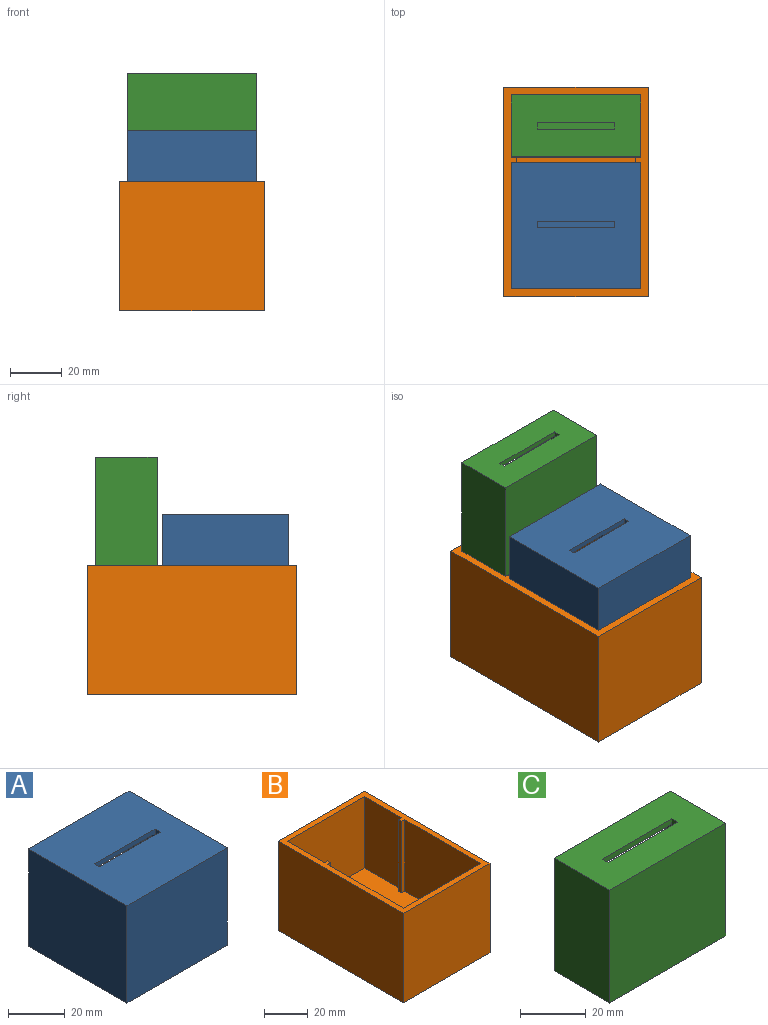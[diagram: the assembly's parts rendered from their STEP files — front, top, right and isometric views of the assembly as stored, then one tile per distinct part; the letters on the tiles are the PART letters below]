
ASSEMBLY  parts=3 mates=2
PART A: 15 faces, bbox 50x49x42 mm
  f0: plane 50x49mm, normal (0,0,1), area 2375mm2, adj f2,f3,f4,f5,f11,f12,f13,f14
  f1: plane 47x46mm, normal (0,0,-1), area 2087mm2, adj f2,f7,f8,f9,f11,f12,f13,f14
  f2: plane 50x42mm, normal (0,1,0), area 352mm2, adj f0,f1,f3,f5,f6,f7,f9,f10
  f3: plane 49x42mm, normal (-1,0,0), area 2058mm2, adj f0,f2,f4,f6
  f4: plane 50x42mm, normal (0,-1,0), area 2100mm2, adj f0,f3,f5,f6
  f5: plane 49x42mm, normal (1,0,0), area 2058mm2, adj f0,f2,f4,f6
  f6: plane 50x49mm, normal (0,0,-1), area 2450mm2, adj f2,f3,f4,f5
  f7: plane 47x38mm, normal (1,0,0), area 1786mm2, adj f1,f2,f8,f10
  f8: plane 46x38mm, normal (0,1,0), area 1748mm2, adj f1,f7,f9,f10
  f9: plane 47x38mm, normal (-1,0,0), area 1786mm2, adj f1,f2,f8,f10
  f10: plane 47x46mm, normal (0,0,1), area 2162mm2, adj f2,f7,f8,f9
  f11: plane 2.5x2mm, normal (-1,0,0), area 5mm2, adj f0,f1,f12,f14
  f12: plane 30x2mm, normal (0,-1,0), area 60mm2, adj f0,f1,f11,f13
  f13: plane 2.5x2mm, normal (1,0,0), area 5mm2, adj f0,f1,f12,f14
  f14: plane 30x2mm, normal (0,1,0), area 60mm2, adj f0,f1,f11,f13
PART B: 19 faces, bbox 56x81x50 mm
  f0: plane 40x24mm, normal (-1,0,0), area 960mm2, adj f2,f10,f12,f16
  f1: plane 40x24mm, normal (1,0,0), area 960mm2, adj f2,f10,f12,f13
  f2: plane 50x40mm, normal (0,-1,0), area 2000mm2, adj f0,f1,f10,f12
  f3: plane 49x40mm, normal (-1,0,0), area 1960mm2, adj f4,f10,f12,f17
  f4: plane 50x40mm, normal (0,1,0), area 2000mm2, adj f3,f9,f10,f12
  f5: plane 56x50mm, normal (0,1,0), area 2800mm2, adj f6,f8,f10,f11
  f6: plane 81x50mm, normal (-1,0,0), area 4050mm2, adj f5,f7,f10,f11
  f7: plane 56x50mm, normal (0,-1,0), area 2800mm2, adj f6,f8,f10,f11
  f8: plane 81x50mm, normal (1,0,0), area 4050mm2, adj f5,f7,f10,f11
  f9: plane 49x40mm, normal (1,0,0), area 1960mm2, adj f4,f10,f12,f14
  f10: plane 81x56mm, normal (0,0,1), area 794mm2, adj f0,f1,f2,f3,f4,f5,f6,f7
  f11: plane 81x56mm, normal (0,0,-1), area 4536mm2, adj f5,f6,f7,f8
  f12: plane 75x50mm, normal (0,0,1), area 3742mm2, adj f0,f1,f2,f3,f4,f9,f13,f14
  f13: plane 40x2mm, normal (0,1,0), area 80mm2, adj f1,f10,f12,f15
  f14: plane 40x2mm, normal (0,-1,0), area 80mm2, adj f9,f10,f12,f15
  f15: plane 40x2mm, normal (1,0,0), area 80mm2, adj f10,f12,f13,f14
  f16: plane 40x2mm, normal (0,1,0), area 80mm2, adj f0,f10,f12,f18
  f17: plane 40x2mm, normal (0,-1,0), area 80mm2, adj f3,f10,f12,f18
  f18: plane 40x2mm, normal (-1,0,0), area 80mm2, adj f10,f12,f16,f17
PART C: 15 faces, bbox 50x24x42 mm
  f0: plane 50x24mm, normal (0,0,1), area 1125mm2, adj f2,f3,f4,f5,f11,f12,f13,f14
  f1: plane 46x22mm, normal (0,0,-1), area 937mm2, adj f2,f7,f8,f9,f11,f12,f13,f14
  f2: plane 50x42mm, normal (0,1,0), area 352mm2, adj f0,f1,f4,f5,f6,f8,f9,f10
  f3: plane 50x42mm, normal (0,-1,0), area 2100mm2, adj f0,f4,f5,f6
  f4: plane 42x24mm, normal (1,0,0), area 1008mm2, adj f0,f2,f3,f6
  f5: plane 42x24mm, normal (-1,0,0), area 1008mm2, adj f0,f2,f3,f6
  f6: plane 50x24mm, normal (0,0,-1), area 1200mm2, adj f2,f3,f4,f5
  f7: plane 46x38mm, normal (0,1,0), area 1748mm2, adj f1,f8,f9,f10
  f8: plane 38x22mm, normal (-1,0,0), area 836mm2, adj f1,f2,f7,f10
  f9: plane 38x22mm, normal (1,0,0), area 836mm2, adj f1,f2,f7,f10
  f10: plane 46x22mm, normal (0,0,1), area 1012mm2, adj f2,f7,f8,f9
  f11: plane 2.5x2mm, normal (-1,0,0), area 5mm2, adj f0,f1,f12,f14
  f12: plane 30x2mm, normal (0,-1,0), area 60mm2, adj f0,f1,f11,f13
  f13: plane 2.5x2mm, normal (1,0,0), area 5mm2, adj f0,f1,f12,f14
  f14: plane 30x2mm, normal (0,1,0), area 60mm2, adj f0,f1,f11,f13
PLACE A t=(-48.25,-6.62,75.29)mm
PLACE B t=(-48.25,-6.62,57.37)mm fixed
PLACE C t=(-48.25,-6.62,97.37)mm
MATE slider B.f12 <-> C.f6  axis (0,0,1) through (-73.25,18.88,67.37)mm
MATE slider B.f12 <-> A.f6  axis (0,0,1) through (-73.25,-19.62,67.37)mm
